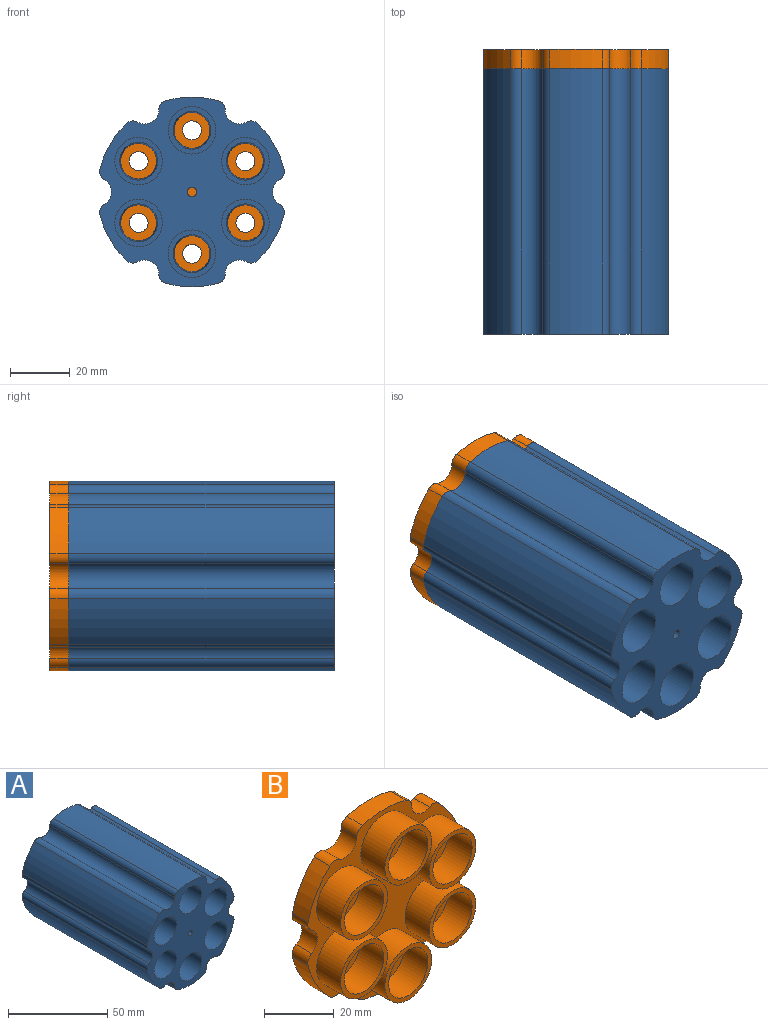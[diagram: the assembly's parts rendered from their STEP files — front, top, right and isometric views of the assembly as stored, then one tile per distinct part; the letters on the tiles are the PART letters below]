
ASSEMBLY  parts=2 mates=1
PART A: 57 faces, bbox 61.8x88.9x63.5 mm
  f0: cylinder r=31.75mm len=88.9mm, axis (0,1,0), area 1589mm2, adj f6,f7,f41,f55
  f1: cylinder r=31.75mm len=88.9mm, axis (0,1,0), area 1589mm2, adj f6,f7,f52,f56
  f2: cylinder r=31.75mm len=88.9mm, axis (0,1,0), area 1589mm2, adj f6,f7,f49,f53
  f3: cylinder r=31.75mm len=88.9mm, axis (0,1,0), area 1589mm2, adj f6,f7,f46,f50
  f4: cylinder r=31.75mm len=88.9mm, axis (0,1,0), area 1589mm2, adj f6,f7,f43,f47
  f5: cylinder r=31.75mm len=88.9mm, axis (0,1,0), area 1589mm2, adj f6,f7,f40,f44
  f6: plane 63.5x61.83mm, normal (0,-1,0), area 1748mm2, adj f0,f1,f2,f3,f4,f5,f8,f11
  f7: plane 63.5x61.83mm, normal (0,1,0), area 1225.5mm2, adj f0,f1,f2,f3,f4,f5,f11,f12
  f8: cylinder r=7.94mm len=20.64mm, axis (0,-1,0), area 1029.2mm2, adj f6,f9
  f9: plane 15.88x15.88mm, normal (0,-1,0), area 71.3mm2, adj f8,f10
  f10: cone r=6.35mm half-angle=0.4deg, axis (0,-1,0), area 2155.8mm2, adj f9,f13
  f11: cylinder r=1.59mm len=88.9mm, axis (0,-1,0), area 886.7mm2, adj f6,f7
  f12: cylinder r=9.53mm len=19.05mm, axis (0,-1,0), area 756.3mm2, adj f7,f13
  f13: plane 19.05x19.05mm, normal (0,1,0), area 172.5mm2, adj f10,f12
  f14: cylinder r=7.94mm len=20.64mm, axis (0,-1,0), area 1029.2mm2, adj f6,f15
  f15: plane 15.88x15.88mm, normal (0,-1,0), area 71.3mm2, adj f14,f16
  f16: cone r=6.35mm half-angle=0.4deg, axis (0,-1,0), area 2155.8mm2, adj f15,f18
  f17: cylinder r=9.53mm len=19.05mm, axis (0,-1,0), area 756.3mm2, adj f7,f18
  f18: plane 19.05x19.05mm, normal (0,1,0), area 172.5mm2, adj f16,f17
  f19: cylinder r=7.94mm len=20.64mm, axis (0,-1,0), area 1029.2mm2, adj f6,f20
  f20: plane 15.88x15.88mm, normal (0,-1,0), area 71.3mm2, adj f19,f21
  f21: cone r=6.35mm half-angle=0.4deg, axis (0,-1,0), area 2155.8mm2, adj f20,f23
  f22: cylinder r=9.53mm len=19.05mm, axis (0,-1,0), area 756.3mm2, adj f7,f23
  f23: plane 19.05x19.05mm, normal (0,1,0), area 172.5mm2, adj f21,f22
  f24: cylinder r=7.94mm len=20.64mm, axis (0,-1,0), area 1029.2mm2, adj f6,f25
  f25: plane 15.88x15.88mm, normal (0,-1,0), area 71.3mm2, adj f24,f26
  f26: cone r=6.35mm half-angle=0.4deg, axis (0,-1,0), area 2155.8mm2, adj f25,f28
  f27: cylinder r=9.53mm len=19.05mm, axis (0,-1,0), area 756.3mm2, adj f7,f28
  f28: plane 19.05x19.05mm, normal (0,1,0), area 172.5mm2, adj f26,f27
  f29: cylinder r=7.94mm len=20.64mm, axis (0,-1,0), area 1029.2mm2, adj f6,f30
  f30: plane 15.88x15.88mm, normal (0,-1,0), area 71.3mm2, adj f29,f31
  f31: cone r=6.35mm half-angle=0.4deg, axis (0,-1,0), area 2155.8mm2, adj f30,f33
  f32: cylinder r=9.53mm len=19.05mm, axis (0,-1,0), area 756.3mm2, adj f7,f33
  f33: plane 19.05x19.05mm, normal (0,1,0), area 172.5mm2, adj f31,f32
  f34: cylinder r=7.94mm len=20.64mm, axis (0,-1,0), area 1029.2mm2, adj f6,f35
  f35: plane 15.88x15.88mm, normal (0,-1,0), area 71.3mm2, adj f34,f36
  f36: cone r=6.35mm half-angle=0.4deg, axis (0,-1,0), area 2155.8mm2, adj f35,f38
  f37: cylinder r=9.53mm len=19.05mm, axis (0,-1,0), area 756.3mm2, adj f7,f38
  f38: plane 19.05x19.05mm, normal (0,1,0), area 172.5mm2, adj f36,f37
  f39: cylinder r=4.76mm len=88.9mm, axis (0,-1,0), area 881.8mm2, adj f6,f7,f40,f41
  f40: cylinder r=3.17mm len=88.9mm, axis (0,1,0), area 362.3mm2, adj f5,f6,f7,f39
  f41: cylinder r=3.17mm len=88.9mm, axis (0,-1,0), area 362.3mm2, adj f0,f6,f7,f39
  f42: cylinder r=4.76mm len=88.9mm, axis (0,-1,0), area 881.8mm2, adj f6,f7,f43,f44
  f43: cylinder r=3.17mm len=88.9mm, axis (0,1,0), area 362.3mm2, adj f4,f6,f7,f42
  f44: cylinder r=3.17mm len=88.9mm, axis (0,-1,0), area 362.3mm2, adj f5,f6,f7,f42
  f45: cylinder r=4.76mm len=88.9mm, axis (0,-1,0), area 881.8mm2, adj f6,f7,f46,f47
  f46: cylinder r=3.17mm len=88.9mm, axis (0,1,0), area 362.3mm2, adj f3,f6,f7,f45
  f47: cylinder r=3.17mm len=88.9mm, axis (0,-1,0), area 362.3mm2, adj f4,f6,f7,f45
  f48: cylinder r=4.76mm len=88.9mm, axis (0,-1,0), area 881.8mm2, adj f6,f7,f49,f50
  f49: cylinder r=3.17mm len=88.9mm, axis (0,1,0), area 362.3mm2, adj f2,f6,f7,f48
  f50: cylinder r=3.17mm len=88.9mm, axis (0,-1,0), area 362.3mm2, adj f3,f6,f7,f48
  f51: cylinder r=4.76mm len=88.9mm, axis (0,-1,0), area 881.8mm2, adj f6,f7,f52,f53
  f52: cylinder r=3.17mm len=88.9mm, axis (0,1,0), area 362.3mm2, adj f1,f6,f7,f51
  f53: cylinder r=3.17mm len=88.9mm, axis (0,-1,0), area 362.3mm2, adj f2,f6,f7,f51
  f54: cylinder r=4.76mm len=88.9mm, axis (0,-1,0), area 881.8mm2, adj f6,f7,f55,f56
  f55: cylinder r=3.17mm len=88.9mm, axis (0,1,0), area 362.3mm2, adj f0,f6,f7,f54
  f56: cylinder r=3.17mm len=88.9mm, axis (0,-1,0), area 362.3mm2, adj f1,f6,f7,f54
PART B: 56 faces, bbox 61.8x16.1x63.5 mm
  f0: plane 15.88x15.88mm, normal (0,-1,0), area 166.3mm2, adj f52,f53
  f1: plane 15.88x15.88mm, normal (0,-1,0), area 166.3mm2, adj f48,f49
  f2: plane 15.88x15.88mm, normal (0,-1,0), area 166.3mm2, adj f44,f45
  f3: plane 15.88x15.88mm, normal (0,-1,0), area 166.3mm2, adj f40,f41
  f4: plane 15.88x15.88mm, normal (0,-1,0), area 166.3mm2, adj f36,f37
  f5: plane 15.88x15.88mm, normal (0,-1,0), area 166.3mm2, adj f32,f33
  f6: cylinder r=31.75mm len=15.28mm, axis (0,1,0), area 113.5mm2, adj f12,f13,f16,f30
  f7: cylinder r=31.75mm len=15.28mm, axis (0,1,0), area 113.5mm2, adj f12,f13,f27,f31
  f8: cylinder r=31.75mm len=17.64mm, axis (0,1,0), area 113.5mm2, adj f12,f13,f24,f28
  f9: cylinder r=31.75mm len=15.28mm, axis (0,1,0), area 113.5mm2, adj f12,f13,f21,f25
  f10: cylinder r=31.75mm len=15.28mm, axis (0,1,0), area 113.5mm2, adj f12,f13,f18,f22
  f11: cylinder r=31.75mm len=17.64mm, axis (0,1,0), area 113.5mm2, adj f12,f13,f15,f19
  f12: plane 63.5x61.83mm, normal (0,-1,0), area 1256.1mm2, adj f6,f7,f8,f9,f10,f11,f14,f15
  f13: plane 63.5x61.83mm, normal (0,1,0), area 2753.5mm2, adj f6,f7,f8,f9,f10,f11,f14,f15
  f14: cylinder r=4.76mm len=7.12mm, axis (0,-1,0), area 63mm2, adj f12,f13,f15,f16
  f15: cylinder r=3.17mm len=6.35mm, axis (0,1,0), area 25.9mm2, adj f11,f12,f13,f14
  f16: cylinder r=3.17mm len=6.35mm, axis (0,-1,0), area 25.9mm2, adj f6,f12,f13,f14
  f17: cylinder r=4.76mm len=7.12mm, axis (0,-1,0), area 63mm2, adj f12,f13,f18,f19
  f18: cylinder r=3.17mm len=6.35mm, axis (0,1,0), area 25.9mm2, adj f10,f12,f13,f17
  f19: cylinder r=3.17mm len=6.35mm, axis (0,-1,0), area 25.9mm2, adj f11,f12,f13,f17
  f20: cylinder r=4.76mm len=8.22mm, axis (0,-1,0), area 63mm2, adj f12,f13,f21,f22
  f21: cylinder r=3.17mm len=6.35mm, axis (0,1,0), area 25.9mm2, adj f9,f12,f13,f20
  f22: cylinder r=3.17mm len=6.35mm, axis (0,-1,0), area 25.9mm2, adj f10,f12,f13,f20
  f23: cylinder r=4.76mm len=7.12mm, axis (0,-1,0), area 63mm2, adj f12,f13,f24,f25
  f24: cylinder r=3.17mm len=6.35mm, axis (0,1,0), area 25.9mm2, adj f8,f12,f13,f23
  f25: cylinder r=3.17mm len=6.35mm, axis (0,-1,0), area 25.9mm2, adj f9,f12,f13,f23
  f26: cylinder r=4.76mm len=7.12mm, axis (0,-1,0), area 63mm2, adj f12,f13,f27,f28
  f27: cylinder r=3.17mm len=6.35mm, axis (0,1,0), area 25.9mm2, adj f7,f12,f13,f26
  f28: cylinder r=3.17mm len=6.35mm, axis (0,-1,0), area 25.9mm2, adj f8,f12,f13,f26
  f29: cylinder r=4.76mm len=8.22mm, axis (0,-1,0), area 63mm2, adj f12,f13,f30,f31
  f30: cylinder r=3.17mm len=6.35mm, axis (0,1,0), area 25.9mm2, adj f6,f12,f13,f29
  f31: cylinder r=3.17mm len=6.35mm, axis (0,-1,0), area 25.9mm2, adj f7,f12,f13,f29
  f32: cylinder r=3.17mm len=6.35mm, axis (0,-1,0), area 126.7mm2, adj f5,f13
  f33: cylinder r=7.94mm len=15.88mm, axis (0,1,0), area 483.9mm2, adj f5,f35
  f34: cylinder r=9.46mm len=18.92mm, axis (0,1,0), area 576.8mm2, adj f12,f35
  f35: plane 18.92x18.92mm, normal (0,-1,0), area 83.3mm2, adj f33,f34
  f36: cylinder r=3.17mm len=6.35mm, axis (0,-1,0), area 126.7mm2, adj f4,f13
  f37: cylinder r=7.94mm len=15.88mm, axis (0,1,0), area 483.9mm2, adj f4,f39
  f38: cylinder r=9.46mm len=18.92mm, axis (0,1,0), area 576.8mm2, adj f12,f39
  f39: plane 18.92x18.92mm, normal (0,-1,0), area 83.3mm2, adj f37,f38
  f40: cylinder r=3.17mm len=6.35mm, axis (0,-1,0), area 126.7mm2, adj f3,f13
  f41: cylinder r=7.94mm len=15.88mm, axis (0,1,0), area 483.9mm2, adj f3,f43
  f42: cylinder r=9.46mm len=18.92mm, axis (0,1,0), area 576.8mm2, adj f12,f43
  f43: plane 18.92x18.92mm, normal (0,-1,0), area 83.3mm2, adj f41,f42
  f44: cylinder r=3.17mm len=6.35mm, axis (0,-1,0), area 126.7mm2, adj f2,f13
  f45: cylinder r=7.94mm len=15.88mm, axis (0,1,0), area 483.9mm2, adj f2,f47
  f46: cylinder r=9.46mm len=18.92mm, axis (0,1,0), area 576.8mm2, adj f12,f47
  f47: plane 18.92x18.92mm, normal (0,-1,0), area 83.3mm2, adj f45,f46
  f48: cylinder r=3.17mm len=6.35mm, axis (0,-1,0), area 126.7mm2, adj f1,f13
  f49: cylinder r=7.94mm len=15.88mm, axis (0,1,0), area 483.9mm2, adj f1,f51
  f50: cylinder r=9.46mm len=18.92mm, axis (0,1,0), area 576.8mm2, adj f12,f51
  f51: plane 18.92x18.92mm, normal (0,-1,0), area 83.3mm2, adj f49,f50
  f52: cylinder r=3.17mm len=6.35mm, axis (0,-1,0), area 126.7mm2, adj f0,f13
  f53: cylinder r=7.94mm len=15.88mm, axis (0,1,0), area 483.9mm2, adj f0,f55
  f54: cylinder r=9.46mm len=18.92mm, axis (0,1,0), area 576.8mm2, adj f12,f55
  f55: plane 18.92x18.92mm, normal (0,-1,0), area 83.3mm2, adj f53,f54
PLACE A t=(0.63,18.43,31.86)mm fixed
PLACE B t=(0.63,24.78,31.86)mm
MATE fastened A.f0 <-> B.f6  axis (0,1,0) through (0.63,18.43,31.86)mm
